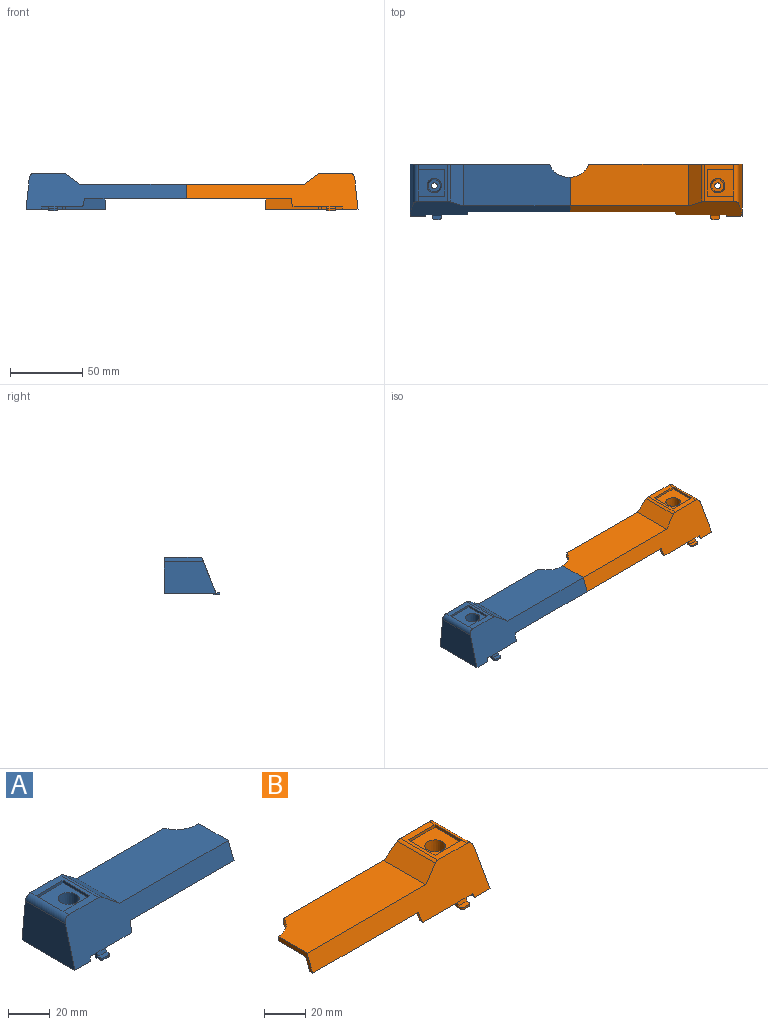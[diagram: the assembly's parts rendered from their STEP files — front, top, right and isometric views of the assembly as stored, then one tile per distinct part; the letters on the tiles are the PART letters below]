
ASSEMBLY  parts=2 mates=1
PART A: 87 faces, bbox 111.1x38.7x25.9 mm
  f0: plane 54.63x36mm, normal (0,0,-1), area 265mm2, adj f2,f6,f16,f22,f29,f30,f31,f43
  f1: plane 11.51x1mm, normal (0,0,-1), area 11.5mm2, adj f2,f3,f4,f20
  f2: plane 23x14.88mm, normal (0,0.93,-0.37), area 332.4mm2, adj f0,f1,f3,f4,f5,f12,f14,f15
  f3: plane 18x11.51mm, normal (-1,0,0), area 131.1mm2, adj f1,f2,f8,f20,f23,f81
  f4: plane 18x11.49mm, normal (1,0,0), area 130.7mm2, adj f1,f2,f5,f7,f20,f37
  f5: plane 9.87x3.39mm, normal (0,0.04,-1), area 31.3mm2, adj f2,f4,f7,f10,f11,f79,f80,f83
  f6: plane 23x22mm, normal (1,0,0), area 483.9mm2, adj f0,f8,f21,f22,f23,f51,f52,f53
  f7: plane 8.22x7.01mm, normal (0,1,0), area 57.6mm2, adj f4,f5,f11,f37
  f8: plane 11.98x7.01mm, normal (0,1,0), area 83.9mm2, adj f3,f6,f23,f81
  f9: plane 22.73x12.85mm, normal (1,0,0), area 292mm2, adj f13,f43,f47,f83
  f10: plane 3.2x0.12mm, normal (1,0,0), area 0.2mm2, adj f5,f47,f49
  f11: plane 23x19.85mm, normal (-1,0,0), area 435mm2, adj f5,f7,f13,f19,f22,f37,f57,f58
  f12: plane 2.52x1.32mm, normal (0.98,0,-0.17), area 2.7mm2, adj f2,f16,f17,f29
  f13: plane 22.8x1.72mm, normal (0,0,-1), area 37.6mm2, adj f9,f11,f22,f43,f83,f84,f85,f86
  f14: plane 4.2x1.99mm, normal (0,0,-1), area 8.4mm2, adj f2,f17,f29,f69
  f15: plane 17.46x2mm, normal (0,0,-1), area 34.9mm2, adj f2,f29,f49,f62,f71,f79
  f16: cylinder r=0.5mm len=2.16mm, axis (0,1,0), area 1.4mm2, adj f0,f2,f12,f29
  f17: bspline ~11.34x0.49mm, area 1.4mm2, adj f2,f12,f14,f29
  f18: plane 6x0.85mm, normal (0,0.93,-0.37), area 5.5mm2, adj f2,f69,f71,f72
  f19: plane 12.32x8.08mm, normal (0,0,-1), area 77.7mm2, adj f11,f20,f22,f54,f57
  f20: cylinder r=6mm len=19.55mm, axis (0,0,1), area 664.9mm2, adj f1,f3,f4,f19,f21,f23,f37,f40
  f21: plane 12.3x12.12mm, normal (0,0,-1), area 127.3mm2, adj f6,f20,f22,f51,f55
  f22: plane 22x21.2mm, normal (0,-1,0), area 448.3mm2, adj f0,f6,f11,f13,f19,f21,f54,f55
  f23: plane 11.98x9.7mm, normal (0,0,-1), area 93.6mm2, adj f3,f6,f8,f20,f52
  f24: plane 4.6x3.84mm, normal (0.98,0,-0.17), area 9.3mm2, adj f29,f49,f62,f66
  f25: plane 23.97x9.93mm, normal (1,0,0), area 66.1mm2, adj f26,f29,f47,f48,f49,f50
  f26: plane 74x29mm, normal (0,0,1), area 2047mm2, adj f25,f29,f31,f42,f48,f63
  f27: plane 16.97x2mm, normal (0,0,-1), area 32.9mm2, adj f31,f43,f48,f63,f67
  f28: plane 26x20.18mm, normal (0,0,1), area 192.1mm2, adj f29,f31,f32,f34,f35,f60,f61
  f29: plane 111.13x25mm, normal (0,-0.93,0.37), area 1668.6mm2, adj f0,f12,f14,f15,f16,f17,f24,f25
  f30: plane 36x21.87mm, normal (-0.99,0,0.1), area 695.3mm2, adj f0,f29,f31,f60
  f31: plane 96.33x25mm, normal (0,1,0), area 1422.9mm2, adj f0,f26,f27,f28,f30,f42,f44,f45
  f32: plane 18.25x1.55mm, normal (0,1,0), area 28.3mm2, adj f28,f33,f35,f36,f60
  f33: plane 18.25x1.55mm, normal (1,0,0), area 28.3mm2, adj f32,f34,f36,f60
  f34: plane 18.25x1.55mm, normal (0,-1,0), area 28.3mm2, adj f28,f33,f35,f36,f60
  f35: plane 18.25x1.55mm, normal (-1,0,0), area 28.3mm2, adj f28,f32,f34,f36
  f36: plane 18.25x18.25mm, normal (0,0,1), area 254.5mm2, adj f32,f33,f34,f35,f38
  f37: plane 9.68x8.22mm, normal (0,0,-1), area 55.6mm2, adj f4,f7,f11,f20,f58
  f38: cone r=5mm half-angle=2deg, axis (0,0,1), area 584.8mm2, adj f36,f39
  f39: plane 8.6x8.6mm, normal (0,0,1), area 45.6mm2, adj f38,f41
  f40: plane 12x12mm, normal (0,0,-1), area 100.5mm2, adj f20,f41
  f41: cylinder r=2mm len=4mm, axis (0,0,-1), area 12.6mm2, adj f39,f40
  f42: plane 29x9.07mm, normal (0.6,0,0.8), area 313.3mm2, adj f26,f29,f31,f61
  f43: plane 70.47x15mm, normal (0,-1,0), area 571.2mm2, adj f0,f9,f13,f27,f44,f45,f46,f47
  f44: plane 9x2mm, normal (1,0,0), area 18mm2, adj f31,f43,f65,f68
  f45: plane 24x2mm, normal (0,0,-1), area 48mm2, adj f31,f43,f64,f68
  f46: plane 2.5x2mm, normal (1,0,0), area 5mm2, adj f31,f43,f64,f67
  f47: plane 84x26mm, normal (0,0,-1), area 2113.1mm2, adj f9,f10,f25,f43,f48,f49,f80
  f48: cylinder r=13.89mm len=14.34mm, axis (0,0,1), area 47.8mm2, adj f25,f26,f27,f43,f47,f63
  f49: plane 84x12.85mm, normal (0,0.93,-0.37), area 747.1mm2, adj f10,f15,f24,f25,f47,f50,f62,f66
  f50: plane 70.25x2mm, normal (0,0,-1), area 140.5mm2, adj f25,f29,f49,f66
  f51: plane 18x6.64mm, normal (0,1,0), area 119.6mm2, adj f6,f20,f21,f53
  f52: plane 18x6.62mm, normal (0,-1,0), area 119.2mm2, adj f6,f20,f23,f53
  f53: plane 6.64x1mm, normal (0,0,-1), area 6.6mm2, adj f6,f20,f51,f52
  f54: plane 18x6.96mm, normal (1,0,0), area 125.3mm2, adj f19,f20,f22,f56
  f55: plane 18x6.96mm, normal (-1,0,0), area 125.3mm2, adj f20,f21,f22,f56
  f56: plane 6.96x1mm, normal (0,0,-1), area 6.9mm2, adj f20,f22,f54,f55
  f57: plane 18x2.62mm, normal (0,1,0), area 47.2mm2, adj f11,f19,f20,f59
  f58: plane 18x2.6mm, normal (0,-1,0), area 46.8mm2, adj f11,f20,f37,f59
  f59: plane 2.62x1mm, normal (0,0,-1), area 2.6mm2, adj f11,f20,f57,f58
  f60: cylinder r=3.5mm len=27.25mm, axis (0,1,0), area 135.2mm2, adj f28,f29,f30,f31,f32,f33,f34
  f61: cylinder r=3.5mm len=26.28mm, axis (0,1,0), area 58.8mm2, adj f28,f29,f31,f42
  f62: cylinder r=0.5mm len=2.17mm, axis (0,1,0), area 1.4mm2, adj f15,f24,f29,f49
  f63: cylinder r=0.5mm len=4mm, axis (0,0,1), area 2.4mm2, adj f26,f27,f31,f48
  f64: cylinder r=0.5mm len=2mm, axis (0,1,0), area 1.6mm2, adj f31,f43,f45,f46
  f65: cylinder r=0.5mm len=2mm, axis (0,-1,0), area 1.6mm2, adj f0,f31,f43,f44
  f66: bspline ~2.38x0.49mm, area 1.4mm2, adj f24,f29,f49,f50
  f67: bspline ~2.2x0.5mm, area 1.6mm2, adj f27,f31,f43,f46
  f68: bspline ~2.2x0.5mm, area 1.6mm2, adj f31,f43,f44,f45
  f69: plane 3.92x3mm, normal (-1,0,0), area 7.1mm2, adj f2,f14,f18,f70,f72,f73,f74,f77
  f70: plane 6x1.83mm, normal (0,-0.93,0.37), area 11.8mm2, adj f29,f69,f71,f73
  f71: plane 3.92x3mm, normal (1,0,0), area 7.1mm2, adj f2,f15,f18,f70,f72,f73,f74,f76
  f72: plane 6x2mm, normal (0,0,-1), area 12mm2, adj f18,f69,f71,f74
  f73: plane 6x2.69mm, normal (0,0,1), area 15.2mm2, adj f69,f70,f71,f75,f76,f77
  f74: plane 6x2.23mm, normal (0,0,-1), area 12.4mm2, adj f69,f71,f72,f75,f76,f77
  f75: plane 3x1.17mm, normal (0,-1,0), area 3.5mm2, adj f73,f74,f76,f77
  f76: cylinder r=1.5mm len=1.5mm, axis (0,0,-1), area 2.8mm2, adj f71,f73,f74,f75
  f77: cylinder r=1.5mm len=1.5mm, axis (0,0,1), area 2.8mm2, adj f69,f73,f74,f75
  f78: plane 15x9.27mm, normal (1,0,0), area 94.4mm2, adj f0,f2,f81,f82
  f79: plane 12.73x5.1mm, normal (-1,0,0), area 0.5mm2, adj f2,f5,f15,f49
  f80: plane 0.12x0mm, normal (-1,0,0), area 0mm2, adj f5,f47,f83
  f81: plane 12.13x3.39mm, normal (0,0.04,-1), area 37.9mm2, adj f2,f3,f6,f8,f78,f82
  f82: plane 15x0.15mm, normal (0,-1,0), area 2.3mm2, adj f0,f6,f78,f81
  f83: plane 12.85x1.65mm, normal (0,-1,0), area 21.2mm2, adj f5,f9,f11,f13,f80
  f84: plane 2.15x0.07mm, normal (1,0,0), area 0.2mm2, adj f0,f13,f22,f86
  f85: plane 2.15x0.07mm, normal (-1,0,0), area 0.2mm2, adj f0,f13,f43,f86
  f86: plane 2.15x1.72mm, normal (0,-1,0), area 3.7mm2, adj f0,f13,f84,f85
PART B: 87 faces, bbox 119.1x38.7x25.9 mm
  f0: plane 63.63x36mm, normal (0,0,-1), area 283mm2, adj f2,f6,f16,f22,f28,f29,f30,f42
  f1: plane 11.51x1mm, normal (0,0,-1), area 11.5mm2, adj f2,f3,f4,f20
  f2: plane 23x14.88mm, normal (0,0.93,-0.37), area 332.4mm2, adj f0,f1,f3,f4,f5,f12,f14,f15
  f3: plane 18x11.51mm, normal (1,0,0), area 131.1mm2, adj f1,f2,f8,f20,f23,f81
  f4: plane 18x11.49mm, normal (-1,0,0), area 130.7mm2, adj f1,f2,f5,f7,f20,f36
  f5: plane 9.87x3.39mm, normal (0,0.04,-1), area 31.3mm2, adj f2,f4,f7,f10,f11,f79,f80,f83
  f6: plane 23x22mm, normal (-1,0,0), area 483.9mm2, adj f0,f8,f21,f22,f23,f51,f52,f53
  f7: plane 8.22x7.01mm, normal (0,1,0), area 57.6mm2, adj f4,f5,f11,f36
  f8: plane 11.98x7.01mm, normal (0,1,0), area 83.9mm2, adj f3,f6,f23,f81
  f9: plane 22.73x12.85mm, normal (-1,0,0), area 292mm2, adj f13,f42,f47,f83
  f10: plane 3.2x0.12mm, normal (-1,0,0), area 0.2mm2, adj f5,f47,f49
  f11: plane 23x19.85mm, normal (1,0,0), area 435mm2, adj f5,f7,f13,f19,f22,f36,f57,f58
  f12: plane 2.52x1.32mm, normal (-0.98,0,-0.17), area 2.7mm2, adj f2,f16,f17,f28
  f13: plane 22.8x1.72mm, normal (0,0,-1), area 37.6mm2, adj f9,f11,f22,f42,f83,f84,f85,f86
  f14: plane 4.2x1.99mm, normal (0,0,-1), area 8.4mm2, adj f2,f17,f28,f69
  f15: plane 23.46x2mm, normal (0,0,-1), area 46.9mm2, adj f2,f28,f49,f62,f71,f79
  f16: cylinder r=0.5mm len=2.16mm, axis (0,1,0), area 1.4mm2, adj f0,f2,f12,f28
  f17: bspline ~11.34x0.49mm, area 1.4mm2, adj f2,f12,f14,f28
  f18: plane 6x0.85mm, normal (0,0.93,-0.37), area 5.5mm2, adj f2,f69,f71,f72
  f19: plane 12.32x8.08mm, normal (0,0,-1), area 77.7mm2, adj f11,f20,f22,f54,f57
  f20: cylinder r=6mm len=19.55mm, axis (0,0,1), area 664.9mm2, adj f1,f3,f4,f19,f21,f23,f36,f39
  f21: plane 12.3x12.12mm, normal (0,0,-1), area 127.3mm2, adj f6,f20,f22,f51,f55
  f22: plane 22x21.2mm, normal (0,-1,0), area 448.3mm2, adj f0,f6,f11,f13,f19,f21,f54,f55
  f23: plane 11.98x9.7mm, normal (0,0,-1), area 93.6mm2, adj f3,f6,f8,f20,f52
  f24: plane 4.6x3.84mm, normal (-0.98,0,-0.17), area 9.3mm2, adj f28,f49,f62,f66
  f25: plane 82x29mm, normal (0,0,1), area 2292.9mm2, adj f28,f30,f41,f46,f48,f63
  f26: plane 17.44x2mm, normal (0,0,-1), area 33.9mm2, adj f30,f42,f48,f63,f67
  f27: plane 26x20.18mm, normal (0,0,1), area 192.1mm2, adj f28,f30,f31,f33,f34,f60,f61
  f28: plane 119.13x25mm, normal (0,-0.93,0.37), area 1789.1mm2, adj f0,f12,f14,f15,f16,f17,f24,f25
  f29: plane 36x21.87mm, normal (0.99,0,0.1), area 695.3mm2, adj f0,f28,f30,f60
  f30: plane 105.79x25mm, normal (0,1,0), area 1582.3mm2, adj f0,f25,f26,f27,f29,f41,f43,f44
  f31: plane 18.25x1.55mm, normal (0,1,0), area 28.3mm2, adj f27,f32,f34,f35,f60
  f32: plane 18.25x1.55mm, normal (-1,0,0), area 28.3mm2, adj f31,f33,f35,f60
  f33: plane 18.25x1.55mm, normal (0,-1,0), area 28.3mm2, adj f27,f32,f34,f35,f60
  f34: plane 18.25x1.55mm, normal (1,0,0), area 28.3mm2, adj f27,f31,f33,f35
  f35: plane 18.25x18.25mm, normal (0,0,1), area 254.5mm2, adj f31,f32,f33,f34,f37
  f36: plane 9.68x8.22mm, normal (0,0,-1), area 55.6mm2, adj f4,f7,f11,f20,f58
  f37: cone r=5mm half-angle=2deg, axis (0,0,1), area 584.8mm2, adj f35,f38
  f38: plane 8.6x8.6mm, normal (0,0,1), area 45.6mm2, adj f37,f40
  f39: plane 12x12mm, normal (0,0,-1), area 100.5mm2, adj f20,f40
  f40: cylinder r=2mm len=4mm, axis (0,0,-1), area 12.6mm2, adj f38,f39
  f41: plane 29x9.07mm, normal (-0.6,0,0.8), area 313.3mm2, adj f25,f28,f30,f61
  f42: plane 79.94x15mm, normal (0,-1,0), area 706.9mm2, adj f0,f9,f13,f26,f43,f44,f45,f47
  f43: plane 9x2mm, normal (-1,0,0), area 18mm2, adj f30,f42,f65,f68
  f44: plane 24x2mm, normal (0,0,-1), area 48mm2, adj f30,f42,f64,f68
  f45: plane 2.5x2mm, normal (-1,0,0), area 5mm2, adj f30,f42,f64,f67
  f46: plane 23.97x9.93mm, normal (-1,0,0), area 66.1mm2, adj f25,f28,f47,f48,f49,f50
  f47: plane 92x26mm, normal (0,0,-1), area 2332.1mm2, adj f9,f10,f42,f46,f48,f49,f80
  f48: cylinder r=13.89mm len=12.88mm, axis (0,0,1), area 44mm2, adj f25,f26,f42,f46,f47,f63
  f49: plane 92x12.85mm, normal (0,0.93,-0.37), area 846.1mm2, adj f10,f15,f24,f46,f47,f50,f62,f66
  f50: plane 72.25x2mm, normal (0,0,-1), area 144.5mm2, adj f28,f46,f49,f66
  f51: plane 18x6.64mm, normal (0,1,0), area 119.6mm2, adj f6,f20,f21,f53
  f52: plane 18x6.62mm, normal (0,-1,0), area 119.2mm2, adj f6,f20,f23,f53
  f53: plane 6.64x1mm, normal (0,0,-1), area 6.6mm2, adj f6,f20,f51,f52
  f54: plane 18x6.96mm, normal (-1,0,0), area 125.3mm2, adj f19,f20,f22,f56
  f55: plane 18x6.96mm, normal (1,0,0), area 125.3mm2, adj f20,f21,f22,f56
  f56: plane 6.96x1mm, normal (0,0,-1), area 6.9mm2, adj f20,f22,f54,f55
  f57: plane 18x2.62mm, normal (0,1,0), area 47.2mm2, adj f11,f19,f20,f59
  f58: plane 18x2.6mm, normal (0,-1,0), area 46.8mm2, adj f11,f20,f36,f59
  f59: plane 2.62x1mm, normal (0,0,-1), area 2.6mm2, adj f11,f20,f57,f58
  f60: cylinder r=3.5mm len=27.25mm, axis (0,1,0), area 135.2mm2, adj f27,f28,f29,f30,f31,f32,f33
  f61: cylinder r=3.5mm len=26.28mm, axis (0,1,0), area 58.8mm2, adj f27,f28,f30,f41
  f62: cylinder r=0.5mm len=2.17mm, axis (0,1,0), area 1.4mm2, adj f15,f24,f28,f49
  f63: cylinder r=0.5mm len=4mm, axis (0,0,1), area 2.4mm2, adj f25,f26,f30,f48
  f64: cylinder r=0.5mm len=2mm, axis (0,1,0), area 1.6mm2, adj f30,f42,f44,f45
  f65: cylinder r=0.5mm len=2mm, axis (0,-1,0), area 1.6mm2, adj f0,f30,f42,f43
  f66: bspline ~2.38x0.49mm, area 1.4mm2, adj f24,f28,f49,f50
  f67: bspline ~2.2x0.5mm, area 1.6mm2, adj f26,f30,f42,f45
  f68: bspline ~2.2x0.5mm, area 1.6mm2, adj f30,f42,f43,f44
  f69: plane 3.92x3mm, normal (1,0,0), area 7.1mm2, adj f2,f14,f18,f70,f72,f73,f74,f77
  f70: plane 6x1.83mm, normal (0,-0.93,0.37), area 11.8mm2, adj f28,f69,f71,f73
  f71: plane 3.92x3mm, normal (-1,0,0), area 7.1mm2, adj f2,f15,f18,f70,f72,f73,f74,f76
  f72: plane 6x2mm, normal (0,0,-1), area 12mm2, adj f18,f69,f71,f74
  f73: plane 6x2.69mm, normal (0,0,1), area 15.2mm2, adj f69,f70,f71,f75,f76,f77
  f74: plane 6x2.23mm, normal (0,0,-1), area 12.4mm2, adj f69,f71,f72,f75,f76,f77
  f75: plane 3x1.17mm, normal (0,-1,0), area 3.5mm2, adj f73,f74,f76,f77
  f76: cylinder r=1.5mm len=1.5mm, axis (0,0,-1), area 2.8mm2, adj f71,f73,f74,f75
  f77: cylinder r=1.5mm len=1.5mm, axis (0,0,1), area 2.8mm2, adj f69,f73,f74,f75
  f78: plane 15x9.27mm, normal (-1,0,0), area 94.4mm2, adj f0,f2,f81,f82
  f79: plane 12.73x5.1mm, normal (1,0,0), area 0.5mm2, adj f2,f5,f15,f49
  f80: plane 0.12x0mm, normal (1,0,0), area 0mm2, adj f5,f47,f83
  f81: plane 12.13x3.39mm, normal (0,0.04,-1), area 37.9mm2, adj f2,f3,f6,f8,f78,f82
  f82: plane 15x0.15mm, normal (0,-1,0), area 2.3mm2, adj f0,f6,f78,f81
  f83: plane 12.85x1.65mm, normal (0,-1,0), area 21.2mm2, adj f5,f9,f11,f13,f80
  f84: plane 2.15x0.07mm, normal (-1,0,0), area 0.2mm2, adj f0,f13,f22,f86
  f85: plane 2.15x0.07mm, normal (1,0,0), area 0.2mm2, adj f0,f13,f42,f86
  f86: plane 2.15x1.72mm, normal (0,-1,0), area 3.7mm2, adj f0,f13,f84,f85
PLACE A t=(115.56,1.87,1.48)mm
PLACE B t=(123.56,1.87,1.48)mm
MATE fastened A.f25 <-> B.f46  axis (1,0,0) through (19.31,-14.13,18.98)mm
